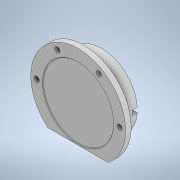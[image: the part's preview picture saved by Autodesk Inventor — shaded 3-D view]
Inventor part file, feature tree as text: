
AUTODESK INVENTOR PART (.ipt)
format: ipt  version: 2020 (Build 240168000, 168)  size: 178,688 bytes
history: native  units: mm
features: extrude x5, sketch x5, other x3, reference x2, plane x1, fillet x1, projected_geometry x1
ambient origin geometry x8: Origin, YZ Plane, XZ Plane, XY Plane, X Axis, Y Axis, Z Axis, Center Point
bodies: 实体1 (feature_tree)
feature tree (18):
  plane  "工作平面1"
  extrude  "拉伸1"  Depth=175.0mm
  extrude  "拉伸2"  Depth=11.0mm TaperAngle=360.0deg
  extrude  "拉伸3"  Depth=10.0mm
  fillet  "圆角1"  Radius=10.0mm
  extrude  "拉伸4"  Depth=38.0mm
  extrude  "拉伸5"  Depth=1.0mm
  sketch  "草图1"  dims[d0=2.0mm d1=175.0mm]
  reference  "参考1"
  reference  "参考2"
  sketch  "草图2"  dims[d2=11.0mm d3=60.0mm d5=360.0deg]
  sketch  "草图3"  dims[d7=12.0mm d8=0.0mm d9=150.0mm d10=10.0mm]
  sketch  "草图4"  dims[d11=38.0mm d12=0.0mm d13=150.0mm]
  sketch  "草图5"  dims[d14=1.0mm d15=0.0mm d16=1.0mm d17=10.0mm d18=200.0mm d19=10.0mm d20=0.0mm d21=3.0mm d22=0.0mm]
  projected_geometry  "投影回路1"
  other  "<userpath>\Desktop\ME_course_project\课设试试\shaft_try_1.iam"
  other  "shaft_try_1.iam"
  other  "xia(1):1"
